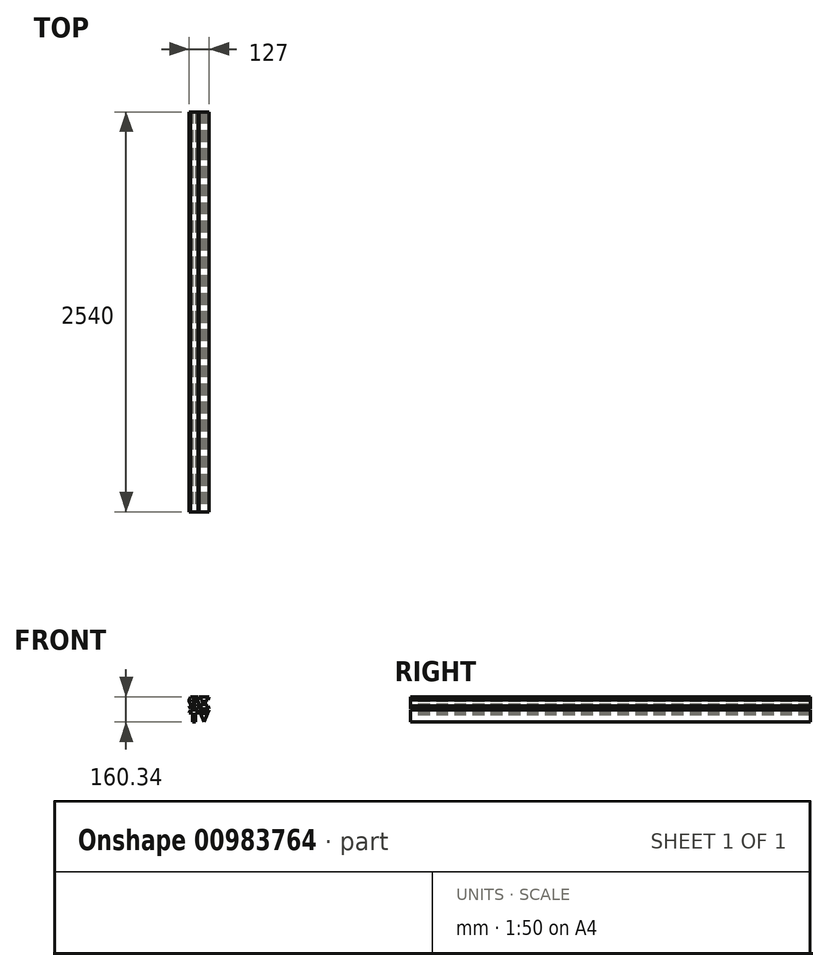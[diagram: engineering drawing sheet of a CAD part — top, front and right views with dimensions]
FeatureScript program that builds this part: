
annotation { "Feature Type Name" : "Feature", "Feature Type Description" : "" }
export const myFeature = defineFeature(function(context is Context, id is Id, definition is map)
    precondition{}
    {
        {
            var Q0;
            Q0=qCreatedBy(makeId("Front.planeOp"),FACE);
            var sketch = newSketch(context, id + "F0", { "sketchPlane" : qUnion([Q0])});
            skLineSegment(sketch, "E0", {"start": v(0, 76.2) * mm, "end": v(-7.94, 76.2) * mm, "construction": true});
            skLineSegment(sketch, "E1", {"start": v(-7.94, 76.2) * mm, "end": v(-55.56, 76.2) * mm});
            skLineSegment(sketch, "E2", {"start": v(-55.56, 76.2) * mm, "end": v(-63.5, 76.2) * mm, "construction": true});
            skLineSegment(sketch, "E3", {"start": v(0, 0) * mm, "end": v(0, 19.05) * mm, "construction": true});
            skLineSegment(sketch, "E4", {"start": v(0, 19.05) * mm, "end": v(0, 28.58) * mm});
            skLineSegment(sketch, "E5", {"start": v(0, 28.58) * mm, "end": v(0, 47.62) * mm, "construction": true});
            skLineSegment(sketch, "E6", {"start": v(0, 47.62) * mm, "end": v(0, 57.15) * mm, "construction": true});
            skLineSegment(sketch, "E7", {"start": v(0, 57.15) * mm, "end": v(0, 76.2) * mm, "construction": true});
            skLineSegment(sketch, "E8", {"start": v(-7.94, 76.2) * mm, "end": v(0, 57.15) * mm});
            skLineSegment(sketch, "E9", {"start": v(0, 0) * mm, "end": v(-7.94, 0) * mm, "construction": true});
            skLineSegment(sketch, "E10", {"start": v(-7.94, 0) * mm, "end": v(-55.56, 0) * mm});
            skLineSegment(sketch, "E11", {"start": v(-55.56, 0) * mm, "end": v(-63.5, 0) * mm, "construction": true});
            skLineSegment(sketch, "E12", {"start": v(-63.5, 76.2) * mm, "end": v(-63.5, 57.15) * mm, "construction": true});
            skLineSegment(sketch, "E13", {"start": v(-63.5, 57.15) * mm, "end": v(-63.5, 47.62) * mm});
            skLineSegment(sketch, "E14", {"start": v(-63.5, 47.62) * mm, "end": v(-63.5, 28.57) * mm, "construction": true});
            skLineSegment(sketch, "E15", {"start": v(-63.5, 28.57) * mm, "end": v(-63.5, 19.05) * mm, "construction": true});
            skLineSegment(sketch, "E16", {"start": v(-63.5, 19.05) * mm, "end": v(-63.5, 0) * mm, "construction": true});
            skLineSegment(sketch, "E17", {"start": v(-63.5, 19.05) * mm, "end": v(-55.56, 0) * mm});
            skLineSegment(sketch, "E18", {"start": v(0, 19.05) * mm, "end": v(-7.94, 0) * mm});
            skLineSegment(sketch, "E19", {"start": v(-55.56, 76.2) * mm, "end": v(-63.5, 57.15) * mm});
            skLineSegment(sketch, "E20", {"start": v(0, 47.62) * mm, "end": v(-7.94, 47.62) * mm, "construction": true});
            skLineSegment(sketch, "E21", {"start": v(-7.94, 47.63) * mm, "end": v(0, 28.57) * mm});
            skLineSegment(sketch, "E22", {"start": v(-63.5, 28.57) * mm, "end": v(-55.56, 28.58) * mm, "construction": true});
            skLineSegment(sketch, "E23", {"start": v(-55.56, 28.58) * mm, "end": v(-63.5, 47.62) * mm});
            skLineSegment(sketch, "E24", {"start": v(-63.5, 19.05) * mm, "end": v(-19.05, 19.05) * mm});
            skLineSegment(sketch, "E25", {"start": v(-19.05, 19.05) * mm, "end": v(-19.05, 28.58) * mm});
            skLineSegment(sketch, "E26", {"start": v(-19.05, 28.58) * mm, "end": v(-55.56, 28.58) * mm});
            skLineSegment(sketch, "E27", {"start": v(0, 57.15) * mm, "end": v(-44.45, 57.15) * mm});
            skLineSegment(sketch, "E28", {"start": v(-44.45, 57.15) * mm, "end": v(-44.45, 47.62) * mm});
            skLineSegment(sketch, "E29", {"start": v(-44.45, 47.62) * mm, "end": v(-7.94, 47.63) * mm});
            skLineSegment(sketch, "E30", {"start": v(0, 0) * mm, "end": v(7.94, 19.05) * mm});
            skLineSegment(sketch, "E31", {"start": v(7.94, 19.05) * mm, "end": v(22.22, 19.05) * mm});
            skLineSegment(sketch, "E32", {"start": v(22.22, 19.05) * mm, "end": v(22.22, 57.15) * mm});
            skLineSegment(sketch, "E33", {"start": v(22.22, 57.15) * mm, "end": v(7.94, 57.15) * mm});
            skLineSegment(sketch, "E34", {"start": v(7.94, 57.15) * mm, "end": v(0, 76.2) * mm});
            skLineSegment(sketch, "E35", {"start": v(0, 76.2) * mm, "end": v(63.5, 76.2) * mm});
            skLineSegment(sketch, "E36", {"start": v(63.5, 76.2) * mm, "end": v(55.56, 57.15) * mm});
            skLineSegment(sketch, "E37", {"start": v(55.56, 57.15) * mm, "end": v(41.27, 57.15) * mm});
            skLineSegment(sketch, "E38", {"start": v(41.27, 57.15) * mm, "end": v(41.27, 19.05) * mm});
            skLineSegment(sketch, "E39", {"start": v(41.27, 19.05) * mm, "end": v(55.56, 19.05) * mm});
            skLineSegment(sketch, "E40", {"start": v(55.56, 19.05) * mm, "end": v(63.5, 0) * mm});
            skLineSegment(sketch, "E41", {"start": v(41.27, 19.05) * mm, "end": v(22.22, 19.05) * mm, "construction": true});
            skLineSegment(sketch, "E42", {"start": v(22.22, 0) * mm, "end": v(22.22, 19.05) * mm, "construction": true});
            skLineSegment(sketch, "E43", {"start": v(22.22, 57.15) * mm, "end": v(41.27, 57.15) * mm, "construction": true});
            skLineSegment(sketch, "E44", {"start": v(22.22, 57.15) * mm, "end": v(22.22, 76.2) * mm, "construction": true});
            skLineSegment(sketch, "E45", {"start": v(0, 0) * mm, "end": v(63.5, 0) * mm});
            skLineSegment(sketch, "E46", {"start": v(0, 0) * mm, "end": v(0, -7.94) * mm, "construction": true});
            skLineSegment(sketch, "E47", {"start": v(0, -7.94) * mm, "end": v(-7.94, -7.94) * mm, "construction": true});
            skLineSegment(sketch, "E48", {"start": v(-7.94, 0) * mm, "end": v(-7.94, -7.94) * mm, "construction": true});
            skLineSegment(sketch, "E49", {"start": v(-7.94, -7.94) * mm, "end": v(-55.56, -7.94) * mm});
            skLineSegment(sketch, "E50", {"start": v(-55.56, -7.94) * mm, "end": v(-55.56, 0) * mm, "construction": true});
            skLineSegment(sketch, "E51", {"start": v(-63.5, 0) * mm, "end": v(-63.5, -7.94) * mm, "construction": true});
            skLineSegment(sketch, "E52", {"start": v(-63.5, -7.94) * mm, "end": v(-55.56, -7.94) * mm, "construction": true});
            skLineSegment(sketch, "E53", {"start": v(-63.5, -7.94) * mm, "end": v(-63.5, -26.99) * mm, "construction": true});
            skLineSegment(sketch, "E54", {"start": v(-63.5, -26.99) * mm, "end": v(-55.56, -7.94) * mm});
            skLineSegment(sketch, "E55", {"start": v(-7.94, -7.94) * mm, "end": v(0, -26.99) * mm});
            skLineSegment(sketch, "E56", {"start": v(0, -26.99) * mm, "end": v(-22.23, -26.99) * mm});
            skLineSegment(sketch, "E57", {"start": v(-22.23, -26.99) * mm, "end": v(-22.22, -84.14) * mm});
            skLineSegment(sketch, "E58", {"start": v(-22.22, -84.14) * mm, "end": v(-41.27, -84.14) * mm});
            skLineSegment(sketch, "E59", {"start": v(-41.27, -84.14) * mm, "end": v(-41.27, -26.99) * mm});
            skLineSegment(sketch, "E60", {"start": v(-41.27, -26.99) * mm, "end": v(-63.5, -26.99) * mm});
            skLineSegment(sketch, "E61", {"start": v(0, -7.94) * mm, "end": v(0, -26.99) * mm, "construction": true});
            skLineSegment(sketch, "E62", {"start": v(-22.23, -26.99) * mm, "end": v(-41.27, -26.99) * mm, "construction": true});
            skLineSegment(sketch, "E63", {"start": v(0, -7.94) * mm, "end": v(31.75, -84.14) * mm});
            skLineSegment(sketch, "E64", {"start": v(31.75, -84.14) * mm, "end": v(63.5, -7.94) * mm});
            skLineSegment(sketch, "E65", {"start": v(63.5, -7.94) * mm, "end": v(44.45, -7.94) * mm});
            skLineSegment(sketch, "E66", {"start": v(44.45, -7.94) * mm, "end": v(19.05, -7.94) * mm, "construction": true});
            skLineSegment(sketch, "E67", {"start": v(19.05, -7.94) * mm, "end": v(0, -7.94) * mm});
            skLineSegment(sketch, "E68", {"start": v(31.75, -7.94) * mm, "end": v(31.75, -84.14) * mm, "construction": true});
            skLineSegment(sketch, "E69", {"start": v(19.05, -7.94) * mm, "end": v(31.75, -38.42) * mm});
            skLineSegment(sketch, "E70", {"start": v(31.75, -38.42) * mm, "end": v(44.45, -7.94) * mm});
            skSolve(sketch);
        }
        {
            var Q0;
            Q0 = qSketchRegion(id + "F0", true);
            extrude(context, id + "F1", {"entities" : qUnion([Q0]), "oppositeDirection" : true, "depth" : 2540 * mm, "offsetDistance" : 25.4 * mm});
        }
    });
